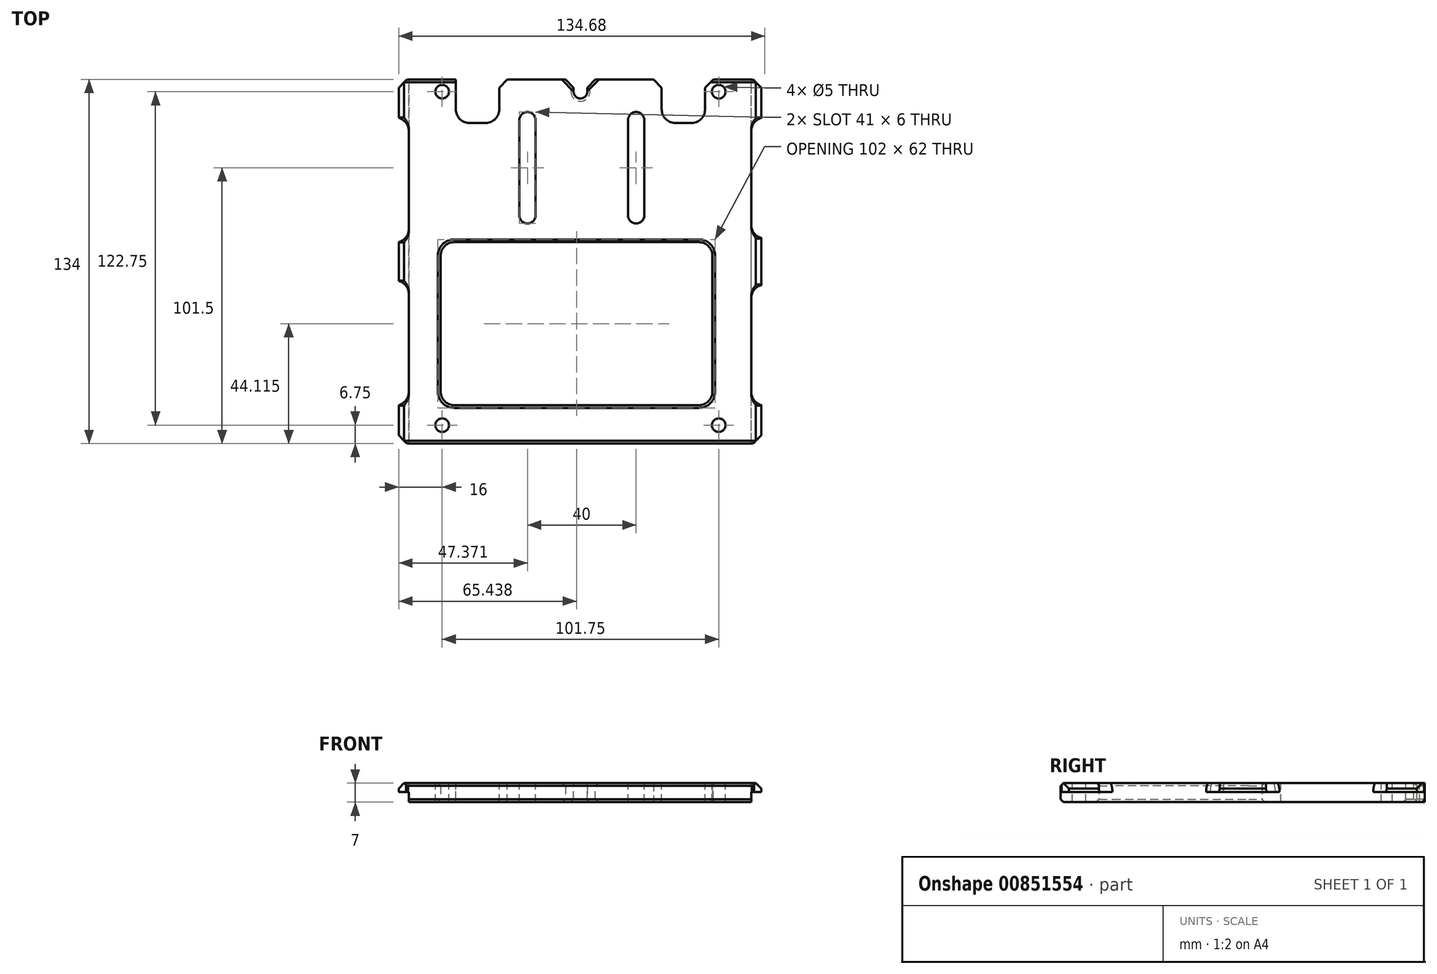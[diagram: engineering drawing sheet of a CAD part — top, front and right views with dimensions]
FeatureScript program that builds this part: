
annotation { "Feature Type Name" : "Feature", "Feature Type Description" : "" }
export const myFeature = defineFeature(function(context is Context, id is Id, definition is map)
    precondition{}
    {
        {
            var Q0;
            Q0=qCreatedBy(makeId("Top.planeOp"),FACE);
            var sketch = newSketch(context, id + "F0", { "sketchPlane" : qUnion([Q0])});
            skLineSegment(sketch, "E0.bottom", {"start": v(0, 0) * mm, "end": v(133.43, 0) * mm});
            skLineSegment(sketch, "E0.top", {"start": v(0, 134) * mm, "end": v(133.43, 134) * mm});
            skLineSegment(sketch, "E0.left", {"start": v(0, 0) * mm, "end": v(0, 134) * mm});
            skLineSegment(sketch, "E0.right", {"start": v(133.43, 0) * mm, "end": v(133.43, 134) * mm});
            skLineSegment(sketch, "E1.bottom", {"start": v(15.44, 74.11) * mm, "end": v(115.44, 74.11) * mm});
            skLineSegment(sketch, "E1.top", {"start": v(15.44, 14.11) * mm, "end": v(115.44, 14.11) * mm});
            skLineSegment(sketch, "E1.left", {"start": v(15.44, 74.11) * mm, "end": v(15.44, 14.11) * mm});
            skLineSegment(sketch, "E1.right", {"start": v(115.44, 74.11) * mm, "end": v(115.44, 14.11) * mm});
            skSolve(sketch);
        }
        {
            var Q0;
            Q0=makeQuery(id+"F0.imprint","IMPRINT",FACE,{"disambiguationData":[TD([[makeQuery(id+"F0.imprint","IMPRINT",EDGE,{"derivedFrom":sQuery(id+"F0.wireOp",EDGE,"E0.bottom")}),1.0]])]});
            extrude(context, id + "F1", {"entities" : qUnion([Q0]), "endBound" : BoundingType.SYMMETRIC, "depth" : 7 * mm, "offsetDistance" : 25 * mm});
        }
        {
            var Q0;
            Q0=makeQuery(id+"F1.opExtrude","CAP_FACE",FACE,{"disambiguationData":[OSD([sQuery(id+"F0.wireOp",EDGE,"E0.bottom"),sQuery(id+"F0.wireOp",EDGE,"E0.top"),sQuery(id+"F0.wireOp",EDGE,"E0.left"),sQuery(id+"F0.wireOp",EDGE,"E0.right")])],"isStart":false});
            var sketch = newSketch(context, id + "F2", { "sketchPlane" : qUnion([Q0])});
            skCircle(sketch, "E2", {"center": v(16, 6.75) * mm, "radius": 2.5 * mm});
            skCircle(sketch, "E3.0.1.0", {"center": v(16, 129.5) * mm, "radius": 2.5 * mm});
            skCircle(sketch, "E3.1.0.0", {"center": v(117.75, 6.75) * mm, "radius": 2.5 * mm});
            skCircle(sketch, "E3.1.1.0", {"center": v(117.75, 129.5) * mm, "radius": 2.5 * mm});
            skLineSegment(sketch, "E3.direction1", {"start": v(16, 6.75) * mm, "end": v(117.75, 6.75) * mm, "construction": true});
            skLineSegment(sketch, "E3.direction2", {"start": v(16, 6.75) * mm, "end": v(16, 129.5) * mm, "construction": true});
            skCircle(sketch, "E4", {"center": v(66.88, 129.5) * mm, "radius": 2.5 * mm});
            skLineSegment(sketch, "E5.bottom", {"start": v(64.38, 129.5) * mm, "end": v(69.34, 129.5) * mm});
            skLineSegment(sketch, "E5.top", {"start": v(64.38, 134) * mm, "end": v(69.34, 134) * mm});
            skLineSegment(sketch, "E5.left", {"start": v(64.38, 129.5) * mm, "end": v(64.38, 134) * mm});
            skLineSegment(sketch, "E5.right", {"start": v(69.34, 129.5) * mm, "end": v(69.34, 134) * mm});
            skLineSegment(sketch, "E6.bottom", {"start": v(21, 134) * mm, "end": v(37, 134) * mm});
            skLineSegment(sketch, "E6.top", {"start": v(21, 118) * mm, "end": v(37, 118) * mm});
            skLineSegment(sketch, "E6.left", {"start": v(21, 134) * mm, "end": v(21, 118) * mm});
            skLineSegment(sketch, "E6.right", {"start": v(37, 134) * mm, "end": v(37, 118) * mm});
            skLineSegment(sketch, "E7.bottom", {"start": v(96.75, 134) * mm, "end": v(112.75, 134) * mm});
            skLineSegment(sketch, "E7.top", {"start": v(96.75, 118) * mm, "end": v(112.75, 118) * mm});
            skLineSegment(sketch, "E7.left", {"start": v(96.75, 134) * mm, "end": v(96.75, 118) * mm});
            skLineSegment(sketch, "E7.right", {"start": v(112.75, 134) * mm, "end": v(112.75, 118) * mm});
            skSolve(sketch);
        }
        {
            var Q0;
            Q0=makeQuery(id+"F2.imprint","IMPRINT",FACE,{"disambiguationData":[TD([[makeQuery(id+"F2.imprint","IMPRINT",EDGE,{"derivedFrom":sQuery(id+"F2.wireOp",EDGE,"E2")}),1.0]])]});
            var Q1;
            Q1=makeQuery(id+"F2.imprint","IMPRINT",FACE,{"disambiguationData":[TD([[makeQuery(id+"F2.imprint","IMPRINT",EDGE,{"derivedFrom":sQuery(id+"F2.wireOp",EDGE,"E3.0.1.0")}),1.0]])]});
            var Q2;
            Q2=makeQuery(id+"F2.imprint","IMPRINT",FACE,{"disambiguationData":[TD([[makeQuery(id+"F2.imprint","IMPRINT",EDGE,{"derivedFrom":sQuery(id+"F2.wireOp",EDGE,"E3.1.1.0")}),1.0]])]});
            var Q3;
            Q3=makeQuery(id+"F2.imprint","IMPRINT",FACE,{"disambiguationData":[TD([[makeQuery(id+"F2.imprint","IMPRINT",EDGE,{"derivedFrom":sQuery(id+"F2.wireOp",EDGE,"E3.1.0.0")}),1.0]])]});
            var Q4;
            Q4=makeQuery(id+"F2.imprint","IMPRINT",FACE,{"disambiguationData":[TD([[makeQuery(id+"F2.imprint","IMPRINT",EDGE,{"derivedFrom":sQuery(id+"F2.wireOp",EDGE,"E4")}),1.0]])]});
            var Q5;
            {var subQ4=sQuery(id+"F2.wireOp",EDGE,"E5.top");Q5=makeQuery(id+"F2.imprint","IMPRINT",FACE,{"disambiguationData":[TD([[makeQuery(id+"F2.imprint","IMPRINT",EDGE,{"derivedFrom":subQ4}),-1.0]])]});}
            var Q6;
            Q6=makeQuery(id+"F2.imprint","IMPRINT",FACE,{"disambiguationData":[TD([[makeQuery(id+"F2.imprint","IMPRINT",EDGE,{"derivedFrom":sQuery(id+"F2.wireOp",EDGE,"E6.bottom")}),-1.0]])]});
            var Q7;
            Q7=makeQuery(id+"F2.imprint","IMPRINT",FACE,{"disambiguationData":[TD([[makeQuery(id+"F2.imprint","IMPRINT",EDGE,{"derivedFrom":sQuery(id+"F2.wireOp",EDGE,"E7.bottom")}),-1.0]])]});
            extrude(context, id + "F3", {"entities" : qUnion([Q0, Q1, Q2, Q3, Q4, Q5, Q6, Q7]), "operationType" : NewBodyOperationType.REMOVE, "oppositeDirection" : true, "depth" : 25 * mm, "offsetDistance" : 25 * mm});
        }
        {
            var Q0;
            Q0=makeQuery(id+"F1.opExtrude","CAP_FACE",FACE,{"disambiguationData":[OSD([sQuery(id+"F0.wireOp",EDGE,"E0.bottom"),sQuery(id+"F0.wireOp",EDGE,"E0.top"),sQuery(id+"F0.wireOp",EDGE,"E0.left"),sQuery(id+"F0.wireOp",EDGE,"E0.right")])],"isStart":false});
            var sketch = newSketch(context, id + "F4", { "sketchPlane" : qUnion([Q0])});
            skLineSegment(sketch, "E8.bottom", {"start": v(0, 120) * mm, "end": v(3.75, 120) * mm});
            skLineSegment(sketch, "E8.top", {"start": v(0, 74) * mm, "end": v(3.75, 74) * mm});
            skLineSegment(sketch, "E8.left", {"start": v(0, 120) * mm, "end": v(0, 74) * mm});
            skLineSegment(sketch, "E8.right", {"start": v(3.75, 120) * mm, "end": v(3.75, 74) * mm});
            skLineSegment(sketch, "E9.bottom", {"start": v(0, 14) * mm, "end": v(3.75, 14) * mm});
            skLineSegment(sketch, "E9.top", {"start": v(0, 60) * mm, "end": v(3.75, 60) * mm});
            skLineSegment(sketch, "E9.left", {"start": v(0, 14) * mm, "end": v(0, 60) * mm});
            skLineSegment(sketch, "E9.right", {"start": v(3.75, 14) * mm, "end": v(3.75, 60) * mm});
            skLineSegment(sketch, "E10.bottom", {"start": v(133.43, 120) * mm, "end": v(129.68, 120) * mm});
            skLineSegment(sketch, "E10.top", {"start": v(133.43, 75.5) * mm, "end": v(129.68, 75.5) * mm});
            skLineSegment(sketch, "E10.left", {"start": v(133.43, 120) * mm, "end": v(133.43, 75.5) * mm});
            skLineSegment(sketch, "E10.right", {"start": v(129.68, 120) * mm, "end": v(129.68, 75.5) * mm});
            skLineSegment(sketch, "E11.bottom", {"start": v(133.43, 14) * mm, "end": v(129.68, 14) * mm});
            skLineSegment(sketch, "E11.top", {"start": v(133.43, 58.5) * mm, "end": v(129.68, 58.5) * mm});
            skLineSegment(sketch, "E11.left", {"start": v(133.43, 14) * mm, "end": v(133.43, 58.5) * mm});
            skLineSegment(sketch, "E11.right", {"start": v(129.68, 14) * mm, "end": v(129.68, 58.5) * mm});
            skSolve(sketch);
        }
        {
            var Q0;
            Q0=makeQuery(id+"F4.imprint","IMPRINT",FACE,{"disambiguationData":[TD([[makeQuery(id+"F4.imprint","IMPRINT",EDGE,{"derivedFrom":sQuery(id+"F4.wireOp",EDGE,"E8.bottom")}),-1.0]])]});
            var Q1;
            Q1=makeQuery(id+"F4.imprint","IMPRINT",FACE,{"disambiguationData":[TD([[makeQuery(id+"F4.imprint","IMPRINT",EDGE,{"derivedFrom":sQuery(id+"F4.wireOp",EDGE,"E9.bottom")}),1.0]])]});
            var Q2;
            Q2=makeQuery(id+"F4.imprint","IMPRINT",FACE,{"disambiguationData":[TD([[makeQuery(id+"F4.imprint","IMPRINT",EDGE,{"derivedFrom":sQuery(id+"F4.wireOp",EDGE,"E11.bottom")}),-1.0]])]});
            var Q3;
            Q3=makeQuery(id+"F4.imprint","IMPRINT",FACE,{"disambiguationData":[TD([[makeQuery(id+"F4.imprint","IMPRINT",EDGE,{"derivedFrom":sQuery(id+"F4.wireOp",EDGE,"E10.bottom")}),1.0]])]});
            extrude(context, id + "F5", {"entities" : qUnion([Q0, Q1, Q2, Q3]), "operationType" : NewBodyOperationType.REMOVE, "oppositeDirection" : true, "depth" : 25 * mm, "offsetDistance" : 25 * mm});
        }
        {
            var Q0;
            Q0=makeQuery(id+"F1.opExtrude","CAP_FACE",FACE,{"disambiguationData":[OSD([sQuery(id+"F0.wireOp",EDGE,"E0.bottom"),sQuery(id+"F0.wireOp",EDGE,"E0.top"),sQuery(id+"F0.wireOp",EDGE,"E0.left"),sQuery(id+"F0.wireOp",EDGE,"E0.right")])],"isStart":true});
            var sketch = newSketch(context, id + "F6", { "sketchPlane" : qUnion([Q0])});
            skLineSegment(sketch, "E12.bottom", {"start": v(0, 0) * mm, "end": v(3.75, 0) * mm});
            skLineSegment(sketch, "E12.top", {"start": v(0, -134) * mm, "end": v(3.75, -134) * mm});
            skLineSegment(sketch, "E12.left", {"start": v(0, 0) * mm, "end": v(0, -134) * mm});
            skLineSegment(sketch, "E12.right", {"start": v(3.75, 0) * mm, "end": v(3.75, -134) * mm});
            skLineSegment(sketch, "E13.bottom", {"start": v(133.43, 0) * mm, "end": v(129.68, 0) * mm});
            skLineSegment(sketch, "E13.top", {"start": v(133.43, -134) * mm, "end": v(129.68, -134) * mm});
            skLineSegment(sketch, "E13.left", {"start": v(133.43, 0) * mm, "end": v(133.43, -134) * mm});
            skLineSegment(sketch, "E13.right", {"start": v(129.68, 0) * mm, "end": v(129.68, -134) * mm});
            skSolve(sketch);
        }
        {
            var Q0;
            Q0=makeQuery(id+"F6.imprint","IMPRINT",FACE,{"disambiguationData":[TD([[makeQuery(id+"F6.imprint","IMPRINT",EDGE,{"derivedFrom":sQuery(id+"F6.wireOp",EDGE,"E12.bottom")}),-1.0]])]});
            var Q1;
            Q1=makeQuery(id+"F6.imprint","IMPRINT",FACE,{"disambiguationData":[TD([[makeQuery(id+"F6.imprint","IMPRINT",EDGE,{"derivedFrom":sQuery(id+"F6.wireOp",EDGE,"E13.bottom")}),-1.0]])]});
            var Q2;
            {var subQ1=makeQuery(id+"F1.opExtrude","CAP_FACE",FACE,{"disambiguationData":[OSD([sQuery(id+"F0.wireOp",EDGE,"E0.bottom"),sQuery(id+"F0.wireOp",EDGE,"E0.top"),sQuery(id+"F0.wireOp",EDGE,"E0.left"),sQuery(id+"F0.wireOp",EDGE,"E0.right")])],"isStart":true});var subQ2=makeQuery(id+"F5.boolean.opBoolean","INTERSECT",EDGE,{"derivedFrom":[subQ1,makeQuery(id+"F5.opExtrude","SWEPT_FACE",FACE,{"disambiguationData":[OSD([sQuery(id+"F4.wireOp",EDGE,"E8.top")])]})]});Q2=makeQuery(id+"F6.imprint","IMPRINT",FACE,{"disambiguationData":[TD([[makeQuery(id+"F6.imprint","IMPRINT",EDGE,{"derivedFrom":subQ2}),1.0]])]});}
            var Q3;
            {var subQ0=sQuery(id+"F6.wireOp",EDGE,"E12.top");Q3=makeQuery(id+"F6.imprint","IMPRINT",FACE,{"disambiguationData":[TD([[makeQuery(id+"F6.imprint","IMPRINT",EDGE,{"derivedFrom":subQ0}),1.0]])]});}
            var Q4;
            {var subQ0=sQuery(id+"F6.wireOp",EDGE,"E13.top");Q4=makeQuery(id+"F6.imprint","IMPRINT",FACE,{"disambiguationData":[TD([[makeQuery(id+"F6.imprint","IMPRINT",EDGE,{"derivedFrom":subQ0}),1.0]])]});}
            var Q5;
            {var subQ1=makeQuery(id+"F1.opExtrude","CAP_FACE",FACE,{"disambiguationData":[OSD([sQuery(id+"F0.wireOp",EDGE,"E0.bottom"),sQuery(id+"F0.wireOp",EDGE,"E0.top"),sQuery(id+"F0.wireOp",EDGE,"E0.left"),sQuery(id+"F0.wireOp",EDGE,"E0.right")])],"isStart":true});var subQ2=makeQuery(id+"F5.boolean.opBoolean","INTERSECT",EDGE,{"derivedFrom":[subQ1,makeQuery(id+"F5.opExtrude","SWEPT_FACE",FACE,{"disambiguationData":[OSD([sQuery(id+"F4.wireOp",EDGE,"E10.top")])]})]});Q5=makeQuery(id+"F6.imprint","IMPRINT",FACE,{"disambiguationData":[TD([[makeQuery(id+"F6.imprint","IMPRINT",EDGE,{"derivedFrom":subQ2}),-1.0]])]});}
            extrude(context, id + "F7", {"entities" : qUnion([Q0, Q1, Q2, Q3, Q4, Q5]), "operationType" : NewBodyOperationType.REMOVE, "oppositeDirection" : true, "depth" : 3.75 * mm, "offsetDistance" : 25 * mm});
        }
        {
            var Q0;
            {var subQ0=sQuery(id+"F0.wireOp",EDGE,"E0.left");var subQ1=sQuery(id+"F0.wireOp",EDGE,"E0.top");Q0=makeQuery(id+"F5.boolean.opBoolean","SPLIT",EDGE,{"disambiguationData":[TD([makeQuery(id+"F1.opExtrude","SWEPT_FACE",FACE,{"disambiguationData":[OSD([subQ1])]})])],"derivedFrom":makeQuery(id+"F1.opExtrude","CAP_EDGE",EDGE,{"disambiguationData":[OSD([subQ0])],"isStart":false})});}
            var Q1;
            {var subQ0=sQuery(id+"F0.wireOp",EDGE,"E0.left");Q1=makeQuery(id+"F5.boolean.opBoolean","SPLIT",EDGE,{"disambiguationData":[TD([makeQuery(id+"F5.opExtrude","SWEPT_FACE",FACE,{"disambiguationData":[OSD([sQuery(id+"F4.wireOp",EDGE,"E8.top")])]})])],"derivedFrom":makeQuery(id+"F1.opExtrude","CAP_EDGE",EDGE,{"disambiguationData":[OSD([subQ0])],"isStart":false})});}
            var Q2;
            {var subQ0=sQuery(id+"F0.wireOp",EDGE,"E0.bottom");var subQ1=sQuery(id+"F0.wireOp",EDGE,"E0.left");Q2=makeQuery(id+"F5.boolean.opBoolean","SPLIT",EDGE,{"disambiguationData":[TD([makeQuery(id+"F1.opExtrude","SWEPT_FACE",FACE,{"disambiguationData":[OSD([subQ0])]})])],"derivedFrom":makeQuery(id+"F1.opExtrude","CAP_EDGE",EDGE,{"disambiguationData":[OSD([subQ1])],"isStart":false})});}
            var Q3;
            {var subQ0=sQuery(id+"F0.wireOp",EDGE,"E0.bottom");var subQ1=sQuery(id+"F0.wireOp",EDGE,"E0.right");Q3=makeQuery(id+"F5.boolean.opBoolean","SPLIT",EDGE,{"disambiguationData":[TD([makeQuery(id+"F1.opExtrude","SWEPT_FACE",FACE,{"disambiguationData":[OSD([subQ0])]})])],"derivedFrom":makeQuery(id+"F1.opExtrude","CAP_EDGE",EDGE,{"disambiguationData":[OSD([subQ1])],"isStart":false})});}
            var Q4;
            {var subQ0=sQuery(id+"F0.wireOp",EDGE,"E0.right");Q4=makeQuery(id+"F5.boolean.opBoolean","SPLIT",EDGE,{"disambiguationData":[TD([makeQuery(id+"F5.opExtrude","SWEPT_FACE",FACE,{"disambiguationData":[OSD([sQuery(id+"F4.wireOp",EDGE,"E10.top")])]})])],"derivedFrom":makeQuery(id+"F1.opExtrude","CAP_EDGE",EDGE,{"disambiguationData":[OSD([subQ0])],"isStart":false})});}
            var Q5;
            {var subQ0=sQuery(id+"F0.wireOp",EDGE,"E0.right");var subQ1=sQuery(id+"F0.wireOp",EDGE,"E0.top");Q5=makeQuery(id+"F5.boolean.opBoolean","SPLIT",EDGE,{"disambiguationData":[TD([makeQuery(id+"F1.opExtrude","SWEPT_FACE",FACE,{"disambiguationData":[OSD([subQ1])]})])],"derivedFrom":makeQuery(id+"F1.opExtrude","CAP_EDGE",EDGE,{"disambiguationData":[OSD([subQ0])],"isStart":false})});}
            chamfer(context, id + "F8", {"entities" : qUnion([Q0, Q1, Q2, Q3, Q4, Q5]), "width" : 2 * mm, "tangentPropagation" : true});
        }
        {
            var Q0;
            Q0=makeQuery(id+"F3.boolean.opBoolean","COPY",EDGE,{"derivedFrom":makeQuery(id+"F3.opExtrude","SWEPT_EDGE",EDGE,{"disambiguationData":[OSD([sQuery(id+"F0.wireOp",EDGE,"E0.top"),sQuery(id+"F2.wireOp",EDGE,"E5.top"),sQuery(id+"F2.wireOp",EDGE,"E5.left")])]})});
            var Q1;
            Q1=makeQuery(id+"F3.boolean.opBoolean","COPY",EDGE,{"derivedFrom":makeQuery(id+"F3.opExtrude","SWEPT_EDGE",EDGE,{"disambiguationData":[OSD([sQuery(id+"F0.wireOp",EDGE,"E0.top"),sQuery(id+"F2.wireOp",EDGE,"E5.top"),sQuery(id+"F2.wireOp",EDGE,"E5.right")])]})});
            var Q2;
            Q2=makeQuery(id+"F1.opExtrude","SWEPT_EDGE",EDGE,{"disambiguationData":[OSD([sQuery(id+"F0.wireOp",EDGE,"E0.top"),sQuery(id+"F0.wireOp",EDGE,"E0.left")])]});
            var Q3;
            Q3=makeQuery(id+"F1.opExtrude","SWEPT_EDGE",EDGE,{"disambiguationData":[OSD([sQuery(id+"F0.wireOp",EDGE,"E0.top"),sQuery(id+"F0.wireOp",EDGE,"E0.right")])]});
            var Q4;
            Q4=makeQuery(id+"F1.opExtrude","SWEPT_EDGE",EDGE,{"disambiguationData":[OSD([sQuery(id+"F0.wireOp",EDGE,"E0.bottom"),sQuery(id+"F0.wireOp",EDGE,"E0.left")])]});
            var Q5;
            Q5=makeQuery(id+"F1.opExtrude","SWEPT_EDGE",EDGE,{"disambiguationData":[OSD([sQuery(id+"F0.wireOp",EDGE,"E0.bottom"),sQuery(id+"F0.wireOp",EDGE,"E0.right")])]});
            var Q6;
            Q6=makeQuery(id+"F3.boolean.opBoolean","COPY",EDGE,{"derivedFrom":makeQuery(id+"F3.opExtrude","SWEPT_EDGE",EDGE,{"disambiguationData":[OSD([sQuery(id+"F0.wireOp",EDGE,"E0.top"),sQuery(id+"F2.wireOp",EDGE,"E6.bottom"),sQuery(id+"F2.wireOp",EDGE,"E6.left")])]})});
            var Q7;
            Q7=makeQuery(id+"F3.boolean.opBoolean","COPY",EDGE,{"derivedFrom":makeQuery(id+"F3.opExtrude","SWEPT_EDGE",EDGE,{"disambiguationData":[OSD([sQuery(id+"F0.wireOp",EDGE,"E0.top"),sQuery(id+"F2.wireOp",EDGE,"E6.bottom"),sQuery(id+"F2.wireOp",EDGE,"E6.right")])]})});
            var Q8;
            Q8=makeQuery(id+"F3.boolean.opBoolean","COPY",EDGE,{"derivedFrom":makeQuery(id+"F3.opExtrude","SWEPT_EDGE",EDGE,{"disambiguationData":[OSD([sQuery(id+"F0.wireOp",EDGE,"E0.top"),sQuery(id+"F2.wireOp",EDGE,"E7.bottom"),sQuery(id+"F2.wireOp",EDGE,"E7.left")])]})});
            var Q9;
            Q9=makeQuery(id+"F3.boolean.opBoolean","COPY",EDGE,{"derivedFrom":makeQuery(id+"F3.opExtrude","SWEPT_EDGE",EDGE,{"disambiguationData":[OSD([sQuery(id+"F0.wireOp",EDGE,"E0.top"),sQuery(id+"F2.wireOp",EDGE,"E7.bottom"),sQuery(id+"F2.wireOp",EDGE,"E7.right")])]})});
            chamfer(context, id + "F9", {"entities" : qUnion([Q0, Q1, Q2, Q3, Q4, Q5, Q6, Q7, Q8, Q9]), "width" : 3 * mm, "tangentPropagation" : true});
        }
        {
            var Q0;
            Q0=makeQuery(id+"F5.boolean.opBoolean","COPY",EDGE,{"derivedFrom":makeQuery(id+"F5.opExtrude","SWEPT_EDGE",EDGE,{"disambiguationData":[OSD([sQuery(id+"F4.wireOp",EDGE,"E8.bottom"),sQuery(id+"F4.wireOp",EDGE,"E8.right")])]})});
            var Q1;
            Q1=makeQuery(id+"F5.boolean.opBoolean","COPY",EDGE,{"derivedFrom":makeQuery(id+"F5.opExtrude","SWEPT_EDGE",EDGE,{"disambiguationData":[OSD([sQuery(id+"F4.wireOp",EDGE,"E8.top"),sQuery(id+"F4.wireOp",EDGE,"E8.right")])]})});
            var Q2;
            Q2=makeQuery(id+"F5.boolean.opBoolean","COPY",EDGE,{"derivedFrom":makeQuery(id+"F5.opExtrude","SWEPT_EDGE",EDGE,{"disambiguationData":[OSD([sQuery(id+"F4.wireOp",EDGE,"E9.bottom"),sQuery(id+"F4.wireOp",EDGE,"E9.right")])]})});
            var Q3;
            Q3=makeQuery(id+"F5.boolean.opBoolean","COPY",EDGE,{"derivedFrom":makeQuery(id+"F5.opExtrude","SWEPT_EDGE",EDGE,{"disambiguationData":[OSD([sQuery(id+"F4.wireOp",EDGE,"E9.top"),sQuery(id+"F4.wireOp",EDGE,"E9.right")])]})});
            var Q4;
            Q4=makeQuery(id+"F5.boolean.opBoolean","COPY",EDGE,{"derivedFrom":makeQuery(id+"F5.opExtrude","SWEPT_EDGE",EDGE,{"disambiguationData":[OSD([sQuery(id+"F4.wireOp",EDGE,"E11.bottom"),sQuery(id+"F4.wireOp",EDGE,"E11.right")])]})});
            var Q5;
            Q5=makeQuery(id+"F5.boolean.opBoolean","COPY",EDGE,{"derivedFrom":makeQuery(id+"F5.opExtrude","SWEPT_EDGE",EDGE,{"disambiguationData":[OSD([sQuery(id+"F4.wireOp",EDGE,"E10.top"),sQuery(id+"F4.wireOp",EDGE,"E10.right")])]})});
            var Q6;
            Q6=makeQuery(id+"F5.boolean.opBoolean","COPY",EDGE,{"derivedFrom":makeQuery(id+"F5.opExtrude","SWEPT_EDGE",EDGE,{"disambiguationData":[OSD([sQuery(id+"F4.wireOp",EDGE,"E10.bottom"),sQuery(id+"F4.wireOp",EDGE,"E10.right")])]})});
            var Q7;
            Q7=makeQuery(id+"F5.boolean.opBoolean","COPY",EDGE,{"derivedFrom":makeQuery(id+"F5.opExtrude","SWEPT_EDGE",EDGE,{"disambiguationData":[OSD([sQuery(id+"F4.wireOp",EDGE,"E11.top"),sQuery(id+"F4.wireOp",EDGE,"E11.right")])]})});
            var Q8;
            Q8=makeQuery(id+"F1.opExtrude","SWEPT_EDGE",EDGE,{"disambiguationData":[OSD([sQuery(id+"F0.wireOp",EDGE,"E1.bottom"),sQuery(id+"F0.wireOp",EDGE,"E1.left")])]});
            var Q9;
            Q9=makeQuery(id+"F1.opExtrude","SWEPT_EDGE",EDGE,{"disambiguationData":[OSD([sQuery(id+"F0.wireOp",EDGE,"E1.top"),sQuery(id+"F0.wireOp",EDGE,"E1.left")])]});
            var Q10;
            Q10=makeQuery(id+"F1.opExtrude","SWEPT_EDGE",EDGE,{"disambiguationData":[OSD([sQuery(id+"F0.wireOp",EDGE,"E1.bottom"),sQuery(id+"F0.wireOp",EDGE,"E1.right")])]});
            var Q11;
            Q11=makeQuery(id+"F1.opExtrude","SWEPT_EDGE",EDGE,{"disambiguationData":[OSD([sQuery(id+"F0.wireOp",EDGE,"E1.top"),sQuery(id+"F0.wireOp",EDGE,"E1.right")])]});
            var Q12;
            Q12=makeQuery(id+"F3.boolean.opBoolean","COPY",EDGE,{"derivedFrom":makeQuery(id+"F3.opExtrude","SWEPT_EDGE",EDGE,{"disambiguationData":[OSD([sQuery(id+"F2.wireOp",EDGE,"E6.top"),sQuery(id+"F2.wireOp",EDGE,"E6.left")])]})});
            var Q13;
            Q13=makeQuery(id+"F3.boolean.opBoolean","COPY",EDGE,{"derivedFrom":makeQuery(id+"F3.opExtrude","SWEPT_EDGE",EDGE,{"disambiguationData":[OSD([sQuery(id+"F2.wireOp",EDGE,"E7.top"),sQuery(id+"F2.wireOp",EDGE,"E7.left")])]})});
            var Q14;
            Q14=makeQuery(id+"F3.boolean.opBoolean","COPY",EDGE,{"derivedFrom":makeQuery(id+"F3.opExtrude","SWEPT_EDGE",EDGE,{"disambiguationData":[OSD([sQuery(id+"F2.wireOp",EDGE,"E6.top"),sQuery(id+"F2.wireOp",EDGE,"E6.right")])]})});
            var Q15;
            Q15=makeQuery(id+"F3.boolean.opBoolean","COPY",EDGE,{"derivedFrom":makeQuery(id+"F3.opExtrude","SWEPT_EDGE",EDGE,{"disambiguationData":[OSD([sQuery(id+"F2.wireOp",EDGE,"E7.top"),sQuery(id+"F2.wireOp",EDGE,"E7.right")])]})});
            fillet(context, id + "F10", {"entities" : qUnion([Q0, Q1, Q2, Q3, Q4, Q5, Q6, Q7, Q8, Q9, Q10, Q11, Q12, Q13, Q14, Q15]), "radius" : 5 * mm, "tangentPropagation" : true, "allowEdgeOverflow" : false});
        }
        {
            var Q0;
            Q0=makeQuery(id+"F1.opExtrude","CAP_EDGE",EDGE,{"disambiguationData":[OSD([sQuery(id+"F0.wireOp",EDGE,"E0.bottom")])],"isStart":false});
            var Q1;
            Q1=makeQuery(id+"F1.opExtrude","CAP_EDGE",EDGE,{"disambiguationData":[OSD([sQuery(id+"F0.wireOp",EDGE,"E0.bottom")])],"isStart":true});
            var Q2;
            Q2=makeQuery(id+"F7.boolean.opBoolean","COPY",EDGE,{"derivedFrom":makeQuery(id+"F7.opExtrude","SWEPT_EDGE",EDGE,{"disambiguationData":[OSD([sQuery(id+"F0.wireOp",EDGE,"E0.bottom"),sQuery(id+"F6.wireOp",EDGE,"E13.bottom"),sQuery(id+"F6.wireOp",EDGE,"E13.right")])]})});
            var Q3;
            Q3=makeQuery(id+"F7.boolean.opBoolean","COPY",EDGE,{"derivedFrom":makeQuery(id+"F7.opExtrude","SWEPT_EDGE",EDGE,{"disambiguationData":[OSD([sQuery(id+"F0.wireOp",EDGE,"E0.bottom"),sQuery(id+"F6.wireOp",EDGE,"E12.bottom"),sQuery(id+"F6.wireOp",EDGE,"E12.right")])]})});
            var Q4;
            Q4=makeQuery(id+"F7.boolean.opBoolean","COPY",EDGE,{"derivedFrom":makeQuery(id+"F7.opExtrude","SWEPT_EDGE",EDGE,{"disambiguationData":[OSD([sQuery(id+"F0.wireOp",EDGE,"E0.top"),sQuery(id+"F6.wireOp",EDGE,"E12.top"),sQuery(id+"F6.wireOp",EDGE,"E12.right")])]})});
            var Q5;
            {var subQ0=sQuery(id+"F0.wireOp",EDGE,"E0.left");var subQ1=sQuery(id+"F0.wireOp",EDGE,"E0.top");Q5=makeQuery(id+"F3.boolean.opBoolean","SPLIT",EDGE,{"disambiguationData":[TD([makeQuery(id+"F1.opExtrude","SWEPT_FACE",FACE,{"disambiguationData":[OSD([subQ0])]})])],"derivedFrom":makeQuery(id+"F1.opExtrude","CAP_EDGE",EDGE,{"disambiguationData":[OSD([subQ1])],"isStart":false})});}
            var Q6;
            Q6=makeQuery(id+"F3.boolean.opBoolean","COPY",EDGE,{"derivedFrom":makeQuery(id+"F3.opExtrude","CAP_EDGE",EDGE,{"disambiguationData":[OSD([sQuery(id+"F2.wireOp",EDGE,"E4")])],"isStart":true})});
            var Q7;
            {var subQ0=sQuery(id+"F0.wireOp",EDGE,"E0.top");Q7=makeQuery(id+"F9.opChamfer","BLEND_EDGE",EDGE,{"blendedFrom":[makeQuery(id+"F3.boolean.opBoolean","COPY",EDGE,{"derivedFrom":makeQuery(id+"F3.opExtrude","SWEPT_EDGE",EDGE,{"disambiguationData":[OSD([subQ0,sQuery(id+"F2.wireOp",EDGE,"E5.top"),sQuery(id+"F2.wireOp",EDGE,"E5.left")])]})}),makeQuery(id+"F1.opExtrude","CAP_FACE",FACE,{"disambiguationData":[OSD([sQuery(id+"F0.wireOp",EDGE,"E0.bottom"),subQ0,sQuery(id+"F0.wireOp",EDGE,"E0.left"),sQuery(id+"F0.wireOp",EDGE,"E0.right")])],"isStart":false})],"blendedInto":[makeQuery(id+"F1.opExtrude","CAP_FACE",FACE,{"disambiguationData":[OSD([sQuery(id+"F0.wireOp",EDGE,"E0.bottom"),subQ0,sQuery(id+"F0.wireOp",EDGE,"E0.left"),sQuery(id+"F0.wireOp",EDGE,"E0.right")])],"isStart":false})]});}
            var Q8;
            {var subQ0=sQuery(id+"F0.wireOp",EDGE,"E0.top");Q8=makeQuery(id+"F9.opChamfer","BLEND_EDGE",EDGE,{"blendedFrom":[makeQuery(id+"F3.boolean.opBoolean","COPY",EDGE,{"derivedFrom":makeQuery(id+"F3.opExtrude","SWEPT_EDGE",EDGE,{"disambiguationData":[OSD([subQ0,sQuery(id+"F2.wireOp",EDGE,"E5.top"),sQuery(id+"F2.wireOp",EDGE,"E5.right")])]})}),makeQuery(id+"F1.opExtrude","CAP_FACE",FACE,{"disambiguationData":[OSD([sQuery(id+"F0.wireOp",EDGE,"E0.bottom"),subQ0,sQuery(id+"F0.wireOp",EDGE,"E0.left"),sQuery(id+"F0.wireOp",EDGE,"E0.right")])],"isStart":false})],"blendedInto":[makeQuery(id+"F1.opExtrude","CAP_FACE",FACE,{"disambiguationData":[OSD([sQuery(id+"F0.wireOp",EDGE,"E0.bottom"),subQ0,sQuery(id+"F0.wireOp",EDGE,"E0.left"),sQuery(id+"F0.wireOp",EDGE,"E0.right")])],"isStart":false})]});}
            var Q9;
            {var subQ0=sQuery(id+"F0.wireOp",EDGE,"E0.top");Q9=makeQuery(id+"F9.opChamfer","BLEND_EDGE",EDGE,{"blendedFrom":[makeQuery(id+"F3.boolean.opBoolean","COPY",EDGE,{"derivedFrom":makeQuery(id+"F3.opExtrude","SWEPT_EDGE",EDGE,{"disambiguationData":[OSD([subQ0,sQuery(id+"F2.wireOp",EDGE,"E5.top"),sQuery(id+"F2.wireOp",EDGE,"E5.right")])]})}),makeQuery(id+"F1.opExtrude","CAP_FACE",FACE,{"disambiguationData":[OSD([sQuery(id+"F0.wireOp",EDGE,"E0.bottom"),subQ0,sQuery(id+"F0.wireOp",EDGE,"E0.left"),sQuery(id+"F0.wireOp",EDGE,"E0.right")])],"isStart":true})],"blendedInto":[makeQuery(id+"F1.opExtrude","CAP_FACE",FACE,{"disambiguationData":[OSD([sQuery(id+"F0.wireOp",EDGE,"E0.bottom"),subQ0,sQuery(id+"F0.wireOp",EDGE,"E0.left"),sQuery(id+"F0.wireOp",EDGE,"E0.right")])],"isStart":true})]});}
            var Q10;
            Q10=makeQuery(id+"F3.boolean.opBoolean","INTERSECT",EDGE,{"derivedFrom":[makeQuery(id+"F1.opExtrude","CAP_FACE",FACE,{"disambiguationData":[OSD([sQuery(id+"F0.wireOp",EDGE,"E0.bottom"),sQuery(id+"F0.wireOp",EDGE,"E0.top"),sQuery(id+"F0.wireOp",EDGE,"E0.left"),sQuery(id+"F0.wireOp",EDGE,"E0.right")])],"isStart":true}),makeQuery(id+"F3.opExtrude","SWEPT_FACE",FACE,{"disambiguationData":[OSD([sQuery(id+"F2.wireOp",EDGE,"E4")])]})]});
            var Q11;
            {var subQ0=sQuery(id+"F0.wireOp",EDGE,"E0.top");Q11=makeQuery(id+"F9.opChamfer","BLEND_EDGE",EDGE,{"blendedFrom":[makeQuery(id+"F3.boolean.opBoolean","COPY",EDGE,{"derivedFrom":makeQuery(id+"F3.opExtrude","SWEPT_EDGE",EDGE,{"disambiguationData":[OSD([subQ0,sQuery(id+"F2.wireOp",EDGE,"E5.top"),sQuery(id+"F2.wireOp",EDGE,"E5.left")])]})}),makeQuery(id+"F1.opExtrude","CAP_FACE",FACE,{"disambiguationData":[OSD([sQuery(id+"F0.wireOp",EDGE,"E0.bottom"),subQ0,sQuery(id+"F0.wireOp",EDGE,"E0.left"),sQuery(id+"F0.wireOp",EDGE,"E0.right")])],"isStart":true})],"blendedInto":[makeQuery(id+"F1.opExtrude","CAP_FACE",FACE,{"disambiguationData":[OSD([sQuery(id+"F0.wireOp",EDGE,"E0.bottom"),subQ0,sQuery(id+"F0.wireOp",EDGE,"E0.left"),sQuery(id+"F0.wireOp",EDGE,"E0.right")])],"isStart":true})]});}
            var Q12;
            {var subQ0=sQuery(id+"F0.wireOp",EDGE,"E0.right");var subQ1=sQuery(id+"F0.wireOp",EDGE,"E0.top");Q12=makeQuery(id+"F3.boolean.opBoolean","SPLIT",EDGE,{"disambiguationData":[TD([makeQuery(id+"F1.opExtrude","SWEPT_FACE",FACE,{"disambiguationData":[OSD([subQ0])]})])],"derivedFrom":makeQuery(id+"F1.opExtrude","CAP_EDGE",EDGE,{"disambiguationData":[OSD([subQ1])],"isStart":false})});}
            var Q13;
            {var subQ0=sQuery(id+"F0.wireOp",EDGE,"E0.right");var subQ1=sQuery(id+"F0.wireOp",EDGE,"E0.top");Q13=makeQuery(id+"F3.boolean.opBoolean","SPLIT",EDGE,{"disambiguationData":[TD([makeQuery(id+"F1.opExtrude","SWEPT_FACE",FACE,{"disambiguationData":[OSD([subQ0])]})])],"derivedFrom":makeQuery(id+"F1.opExtrude","CAP_EDGE",EDGE,{"disambiguationData":[OSD([subQ1])],"isStart":true})});}
            var Q14;
            Q14=makeQuery(id+"F7.boolean.opBoolean","COPY",EDGE,{"derivedFrom":makeQuery(id+"F7.opExtrude","SWEPT_EDGE",EDGE,{"disambiguationData":[OSD([sQuery(id+"F0.wireOp",EDGE,"E0.top"),sQuery(id+"F6.wireOp",EDGE,"E13.top"),sQuery(id+"F6.wireOp",EDGE,"E13.right")])]})});
            var Q15;
            {var subQ0=sQuery(id+"F6.wireOp",EDGE,"E13.right");var subQ1=sQuery(id+"F0.wireOp",EDGE,"E0.right");var subQ2=sQuery(id+"F0.wireOp",EDGE,"E0.top");var subQ3=sQuery(id+"F0.wireOp",EDGE,"E0.bottom");var subQ4=makeQuery(id+"F1.opExtrude","CAP_FACE",FACE,{"disambiguationData":[OSD([subQ3,subQ2,sQuery(id+"F0.wireOp",EDGE,"E0.left"),subQ1])],"isStart":true});var subQ5=subQ4;Q15=makeQuery(id+"F7.boolean.opBoolean","MERGE",EDGE,{"derivedFrom":[makeQuery(id+"F5.boolean.opBoolean","INTERSECT",EDGE,{"derivedFrom":[subQ5,makeQuery(id+"F5.opExtrude","SWEPT_FACE",FACE,{"disambiguationData":[OSD([sQuery(id+"F4.wireOp",EDGE,"E10.right")])]})]}),makeQuery(id+"F5.boolean.opBoolean","INTERSECT",EDGE,{"derivedFrom":[subQ5,makeQuery(id+"F5.opExtrude","SWEPT_FACE",FACE,{"disambiguationData":[OSD([sQuery(id+"F4.wireOp",EDGE,"E11.right")])]})]}),makeQuery(id+"F7.opExtrude","CAP_EDGE",EDGE,{"disambiguationData":[OSD([subQ0]),TDD([makeQuery(id+"F6.imprint","IMPRINT",EDGE,{"disambiguationData":[TD([[makeQuery(id+"F6.imprint","INTERSECT",VERTEX,{"derivedFrom":[makeQuery(id+"F5.boolean.opBoolean","INTERSECT",EDGE,{"derivedFrom":[subQ5,makeQuery(id+"F5.opExtrude","SWEPT_FACE",FACE,{"disambiguationData":[OSD([sQuery(id+"F4.wireOp",EDGE,"E11.bottom")])]})]}),subQ0]}),1.0],[makeQuery(id+"F6.imprint","INTERSECT",VERTEX,{"derivedFrom":[makeQuery(id+"F1.opExtrude","CAP_EDGE",EDGE,{"disambiguationData":[OSD([subQ3])],"isStart":true}),sQuery(id+"F6.wireOp",EDGE,"E13.bottom"),subQ0]}),-1.0]])],"derivedFrom":subQ0})])],"isStart":true}),makeQuery(id+"F7.opExtrude","CAP_EDGE",EDGE,{"disambiguationData":[OSD([subQ0]),TDD([makeQuery(id+"F6.imprint","IMPRINT",EDGE,{"disambiguationData":[TD([[makeQuery(id+"F6.imprint","INTERSECT",VERTEX,{"derivedFrom":[makeQuery(id+"F5.boolean.opBoolean","INTERSECT",EDGE,{"derivedFrom":[subQ5,makeQuery(id+"F5.opExtrude","SWEPT_FACE",FACE,{"disambiguationData":[OSD([sQuery(id+"F4.wireOp",EDGE,"E10.top")])]})]}),subQ0]}),1.0],[makeQuery(id+"F6.imprint","INTERSECT",VERTEX,{"derivedFrom":[makeQuery(id+"F5.boolean.opBoolean","INTERSECT",EDGE,{"derivedFrom":[subQ5,makeQuery(id+"F5.opExtrude","SWEPT_FACE",FACE,{"disambiguationData":[OSD([sQuery(id+"F4.wireOp",EDGE,"E11.top")])]})]}),subQ0]}),-1.0]])],"derivedFrom":subQ0})])],"isStart":true}),makeQuery(id+"F7.opExtrude","CAP_EDGE",EDGE,{"disambiguationData":[OSD([subQ0]),TDD([makeQuery(id+"F6.imprint","IMPRINT",EDGE,{"disambiguationData":[TD([[makeQuery(id+"F6.imprint","INTERSECT",VERTEX,{"derivedFrom":[makeQuery(id+"F5.boolean.opBoolean","INTERSECT",EDGE,{"derivedFrom":[subQ5,makeQuery(id+"F5.opExtrude","SWEPT_FACE",FACE,{"disambiguationData":[OSD([sQuery(id+"F4.wireOp",EDGE,"E10.bottom")])]})]}),subQ0]}),-1.0],[makeQuery(id+"F6.imprint","INTERSECT",VERTEX,{"derivedFrom":[makeQuery(id+"F3.boolean.opBoolean","SPLIT",EDGE,{"disambiguationData":[TD([makeQuery(id+"F1.opExtrude","SWEPT_FACE",FACE,{"disambiguationData":[OSD([subQ1])]})])],"derivedFrom":makeQuery(id+"F1.opExtrude","CAP_EDGE",EDGE,{"disambiguationData":[OSD([subQ2])],"isStart":true})}),sQuery(id+"F6.wireOp",EDGE,"E13.top"),subQ0]}),1.0]])],"derivedFrom":subQ0})])],"isStart":true})]});}
            var Q16;
            {var subQ0=sQuery(id+"F6.wireOp",EDGE,"E12.right");var subQ1=sQuery(id+"F0.wireOp",EDGE,"E0.left");var subQ2=sQuery(id+"F0.wireOp",EDGE,"E0.top");var subQ3=sQuery(id+"F0.wireOp",EDGE,"E0.bottom");var subQ4=makeQuery(id+"F1.opExtrude","CAP_FACE",FACE,{"disambiguationData":[OSD([subQ3,subQ2,subQ1,sQuery(id+"F0.wireOp",EDGE,"E0.right")])],"isStart":true});var subQ5=subQ4;Q16=makeQuery(id+"F7.boolean.opBoolean","MERGE",EDGE,{"derivedFrom":[makeQuery(id+"F5.boolean.opBoolean","INTERSECT",EDGE,{"derivedFrom":[subQ5,makeQuery(id+"F5.opExtrude","SWEPT_FACE",FACE,{"disambiguationData":[OSD([sQuery(id+"F4.wireOp",EDGE,"E8.right")])]})]}),makeQuery(id+"F5.boolean.opBoolean","INTERSECT",EDGE,{"derivedFrom":[subQ5,makeQuery(id+"F5.opExtrude","SWEPT_FACE",FACE,{"disambiguationData":[OSD([sQuery(id+"F4.wireOp",EDGE,"E9.right")])]})]}),makeQuery(id+"F7.opExtrude","CAP_EDGE",EDGE,{"disambiguationData":[OSD([subQ0]),TDD([makeQuery(id+"F6.imprint","IMPRINT",EDGE,{"disambiguationData":[TD([[makeQuery(id+"F6.imprint","INTERSECT",VERTEX,{"derivedFrom":[makeQuery(id+"F5.boolean.opBoolean","INTERSECT",EDGE,{"derivedFrom":[subQ5,makeQuery(id+"F5.opExtrude","SWEPT_FACE",FACE,{"disambiguationData":[OSD([sQuery(id+"F4.wireOp",EDGE,"E9.bottom")])]})]}),subQ0]}),1.0],[makeQuery(id+"F6.imprint","INTERSECT",VERTEX,{"derivedFrom":[makeQuery(id+"F1.opExtrude","CAP_EDGE",EDGE,{"disambiguationData":[OSD([subQ3])],"isStart":true}),sQuery(id+"F6.wireOp",EDGE,"E12.bottom"),subQ0]}),-1.0]])],"derivedFrom":subQ0})])],"isStart":true}),makeQuery(id+"F7.opExtrude","CAP_EDGE",EDGE,{"disambiguationData":[OSD([subQ0]),TDD([makeQuery(id+"F6.imprint","IMPRINT",EDGE,{"disambiguationData":[TD([[makeQuery(id+"F6.imprint","INTERSECT",VERTEX,{"derivedFrom":[makeQuery(id+"F5.boolean.opBoolean","INTERSECT",EDGE,{"derivedFrom":[subQ5,makeQuery(id+"F5.opExtrude","SWEPT_FACE",FACE,{"disambiguationData":[OSD([sQuery(id+"F4.wireOp",EDGE,"E8.top")])]})]}),subQ0]}),1.0],[makeQuery(id+"F6.imprint","INTERSECT",VERTEX,{"derivedFrom":[makeQuery(id+"F5.boolean.opBoolean","INTERSECT",EDGE,{"derivedFrom":[subQ5,makeQuery(id+"F5.opExtrude","SWEPT_FACE",FACE,{"disambiguationData":[OSD([sQuery(id+"F4.wireOp",EDGE,"E9.top")])]})]}),subQ0]}),-1.0]])],"derivedFrom":subQ0})])],"isStart":true}),makeQuery(id+"F7.opExtrude","CAP_EDGE",EDGE,{"disambiguationData":[OSD([subQ0]),TDD([makeQuery(id+"F6.imprint","IMPRINT",EDGE,{"disambiguationData":[TD([[makeQuery(id+"F6.imprint","INTERSECT",VERTEX,{"derivedFrom":[makeQuery(id+"F5.boolean.opBoolean","INTERSECT",EDGE,{"derivedFrom":[subQ5,makeQuery(id+"F5.opExtrude","SWEPT_FACE",FACE,{"disambiguationData":[OSD([sQuery(id+"F4.wireOp",EDGE,"E8.bottom")])]})]}),subQ0]}),-1.0],[makeQuery(id+"F6.imprint","INTERSECT",VERTEX,{"derivedFrom":[makeQuery(id+"F3.boolean.opBoolean","SPLIT",EDGE,{"disambiguationData":[TD([makeQuery(id+"F1.opExtrude","SWEPT_FACE",FACE,{"disambiguationData":[OSD([subQ1])]})])],"derivedFrom":makeQuery(id+"F1.opExtrude","CAP_EDGE",EDGE,{"disambiguationData":[OSD([subQ2])],"isStart":true})}),sQuery(id+"F6.wireOp",EDGE,"E12.top"),subQ0]}),1.0]])],"derivedFrom":subQ0})])],"isStart":true})]});}
            var Q17;
            {var subQ0=sQuery(id+"F0.wireOp",EDGE,"E0.left");var subQ1=sQuery(id+"F0.wireOp",EDGE,"E0.top");Q17=makeQuery(id+"F3.boolean.opBoolean","SPLIT",EDGE,{"disambiguationData":[TD([makeQuery(id+"F1.opExtrude","SWEPT_FACE",FACE,{"disambiguationData":[OSD([subQ0])]})])],"derivedFrom":makeQuery(id+"F1.opExtrude","CAP_EDGE",EDGE,{"disambiguationData":[OSD([subQ1])],"isStart":true})});}
            var Q18;
            {var subQ1=sQuery(id+"F0.wireOp",EDGE,"E0.left");var subQ2=sQuery(id+"F0.wireOp",EDGE,"E0.top");Q18=makeQuery(id+"F9.opChamfer","BLEND_EDGE",EDGE,{"blendedFrom":[makeQuery(id+"F1.opExtrude","SWEPT_EDGE",EDGE,{"disambiguationData":[OSD([subQ2,subQ1])]}),makeQuery(id+"F3.boolean.opBoolean","SPLIT",FACE,{"disambiguationData":[TD([makeQuery(id+"F1.opExtrude","SWEPT_FACE",FACE,{"disambiguationData":[OSD([subQ1])]})])],"derivedFrom":makeQuery(id+"F1.opExtrude","SWEPT_FACE",FACE,{"disambiguationData":[OSD([subQ2])]})})],"blendedInto":[makeQuery(id+"F3.boolean.opBoolean","SPLIT",FACE,{"disambiguationData":[TD([makeQuery(id+"F1.opExtrude","SWEPT_FACE",FACE,{"disambiguationData":[OSD([subQ1])]})])],"derivedFrom":makeQuery(id+"F1.opExtrude","SWEPT_FACE",FACE,{"disambiguationData":[OSD([subQ2])]})})]});}
            var Q19;
            {var subQ0=sQuery(id+"F0.wireOp",EDGE,"E0.bottom");Q19=makeQuery(id+"F9.opChamfer","BLEND_EDGE",EDGE,{"blendedFrom":[makeQuery(id+"F1.opExtrude","SWEPT_EDGE",EDGE,{"disambiguationData":[OSD([subQ0,sQuery(id+"F0.wireOp",EDGE,"E0.left")])]}),makeQuery(id+"F1.opExtrude","SWEPT_FACE",FACE,{"disambiguationData":[OSD([subQ0])]})],"blendedInto":[makeQuery(id+"F1.opExtrude","SWEPT_FACE",FACE,{"disambiguationData":[OSD([subQ0])]})]});}
            var Q20;
            {var subQ0=sQuery(id+"F0.wireOp",EDGE,"E0.bottom");Q20=makeQuery(id+"F9.opChamfer","BLEND_EDGE",EDGE,{"blendedFrom":[makeQuery(id+"F1.opExtrude","SWEPT_EDGE",EDGE,{"disambiguationData":[OSD([subQ0,sQuery(id+"F0.wireOp",EDGE,"E0.right")])]}),makeQuery(id+"F1.opExtrude","SWEPT_FACE",FACE,{"disambiguationData":[OSD([subQ0])]})],"blendedInto":[makeQuery(id+"F1.opExtrude","SWEPT_FACE",FACE,{"disambiguationData":[OSD([subQ0])]})]});}
            var Q21;
            {var subQ0=sQuery(id+"F0.wireOp",EDGE,"E0.right");var subQ2=sQuery(id+"F0.wireOp",EDGE,"E0.top");Q21=makeQuery(id+"F9.opChamfer","BLEND_EDGE",EDGE,{"blendedFrom":[makeQuery(id+"F1.opExtrude","SWEPT_EDGE",EDGE,{"disambiguationData":[OSD([subQ2,subQ0])]}),makeQuery(id+"F3.boolean.opBoolean","SPLIT",FACE,{"disambiguationData":[TD([makeQuery(id+"F1.opExtrude","SWEPT_FACE",FACE,{"disambiguationData":[OSD([subQ0])]})])],"derivedFrom":makeQuery(id+"F1.opExtrude","SWEPT_FACE",FACE,{"disambiguationData":[OSD([subQ2])]})})],"blendedInto":[makeQuery(id+"F3.boolean.opBoolean","SPLIT",FACE,{"disambiguationData":[TD([makeQuery(id+"F1.opExtrude","SWEPT_FACE",FACE,{"disambiguationData":[OSD([subQ0])]})])],"derivedFrom":makeQuery(id+"F1.opExtrude","SWEPT_FACE",FACE,{"disambiguationData":[OSD([subQ2])]})})]});}
            var Q22;
            Q22=makeQuery(id+"F1.opExtrude","CAP_EDGE",EDGE,{"disambiguationData":[OSD([sQuery(id+"F0.wireOp",EDGE,"E1.left")])],"isStart":false});
            var Q23;
            {var subQ0=sQuery(id+"F0.wireOp",EDGE,"E1.left");var subQ1=sQuery(id+"F0.wireOp",EDGE,"E1.top");Q23=makeQuery(id+"F10.opFillet","BLEND_EDGE",EDGE,{"blendedFrom":[makeQuery(id+"F1.opExtrude","SWEPT_EDGE",EDGE,{"disambiguationData":[OSD([subQ1,subQ0])]}),makeQuery(id+"F1.opExtrude","CAP_FACE",FACE,{"disambiguationData":[OSD([sQuery(id+"F0.wireOp",EDGE,"E0.bottom"),sQuery(id+"F0.wireOp",EDGE,"E0.top"),sQuery(id+"F0.wireOp",EDGE,"E0.left"),sQuery(id+"F0.wireOp",EDGE,"E0.right"),sQuery(id+"F0.wireOp",EDGE,"E1.bottom"),subQ1,subQ0,sQuery(id+"F0.wireOp",EDGE,"E1.right")])],"isStart":false})],"blendedInto":[makeQuery(id+"F1.opExtrude","CAP_FACE",FACE,{"disambiguationData":[OSD([sQuery(id+"F0.wireOp",EDGE,"E0.bottom"),sQuery(id+"F0.wireOp",EDGE,"E0.top"),sQuery(id+"F0.wireOp",EDGE,"E0.left"),sQuery(id+"F0.wireOp",EDGE,"E0.right"),sQuery(id+"F0.wireOp",EDGE,"E1.bottom"),subQ1,subQ0,sQuery(id+"F0.wireOp",EDGE,"E1.right")])],"isStart":false})]});}
            var Q24;
            Q24=makeQuery(id+"F1.opExtrude","CAP_EDGE",EDGE,{"disambiguationData":[OSD([sQuery(id+"F0.wireOp",EDGE,"E1.bottom")])],"isStart":true});
            chamfer(context, id + "F11", {"entities" : qUnion([Q0, Q1, Q2, Q3, Q4, Q5, Q6, Q7, Q8, Q9, Q10, Q11, Q12, Q13, Q14, Q15, Q16, Q17, Q18, Q19, Q20, Q21, Q22, Q23, Q24]), "width" : 1 * mm, "tangentPropagation" : true});
        }
        {
            var Q0;
            Q0=makeQuery(id+"F1.opExtrude","CAP_FACE",FACE,{"disambiguationData":[OSD([sQuery(id+"F0.wireOp",EDGE,"E0.bottom"),sQuery(id+"F0.wireOp",EDGE,"E0.top"),sQuery(id+"F0.wireOp",EDGE,"E0.left"),sQuery(id+"F0.wireOp",EDGE,"E0.right")])],"isStart":false});
            var sketch = newSketch(context, id + "F12", { "sketchPlane" : qUnion([Q0])});
            skCircle(sketch, "E14", {"center": v(47.37, 84) * mm, "radius": 3 * mm});
            skCircle(sketch, "E15.0.1.0", {"center": v(47.37, 119) * mm, "radius": 3 * mm});
            skCircle(sketch, "E15.1.0.0", {"center": v(87.37, 84) * mm, "radius": 3 * mm});
            skCircle(sketch, "E15.1.1.0", {"center": v(87.37, 119) * mm, "radius": 3 * mm});
            skLineSegment(sketch, "E15.direction1", {"start": v(47.37, 84) * mm, "end": v(87.37, 84) * mm, "construction": true});
            skLineSegment(sketch, "E15.direction2", {"start": v(47.37, 84) * mm, "end": v(47.37, 119) * mm, "construction": true});
            skCircle(sketch, "E16", {"center": v(47.37, 84) * mm, "radius": 1 * mm});
            skCircle(sketch, "E17.0.1.0", {"center": v(47.37, 119) * mm, "radius": 1 * mm});
            skCircle(sketch, "E17.1.0.0", {"center": v(87.37, 84) * mm, "radius": 1 * mm});
            skCircle(sketch, "E17.1.1.0", {"center": v(87.37, 119) * mm, "radius": 1 * mm});
            skLineSegment(sketch, "E18.bottom", {"start": v(44.37, 119) * mm, "end": v(50.37, 119) * mm});
            skLineSegment(sketch, "E18.top", {"start": v(44.37, 84) * mm, "end": v(50.37, 84) * mm});
            skLineSegment(sketch, "E18.left", {"start": v(44.37, 119) * mm, "end": v(44.37, 84) * mm});
            skLineSegment(sketch, "E18.right", {"start": v(50.37, 119) * mm, "end": v(50.37, 84) * mm});
            skLineSegment(sketch, "E19.bottom", {"start": v(84.37, 119) * mm, "end": v(90.37, 119) * mm});
            skLineSegment(sketch, "E19.top", {"start": v(84.37, 84) * mm, "end": v(90.37, 84) * mm});
            skLineSegment(sketch, "E19.left", {"start": v(84.37, 119) * mm, "end": v(84.37, 84) * mm});
            skLineSegment(sketch, "E19.right", {"start": v(90.37, 119) * mm, "end": v(90.37, 84) * mm});
            skSolve(sketch);
        }
        {
            var Q0;
            Q0=makeQuery(id+"F12.imprint","IMPRINT",FACE,{"disambiguationData":[TD([[makeQuery(id+"F12.imprint","IMPRINT",EDGE,{"derivedFrom":sQuery(id+"F12.wireOp",EDGE,"E15.0.1.0")}),1.0]])]});
            var Q1;
            Q1=makeQuery(id+"F12.imprint","IMPRINT",FACE,{"disambiguationData":[TD([[makeQuery(id+"F12.imprint","IMPRINT",EDGE,{"derivedFrom":sQuery(id+"F12.wireOp",EDGE,"E14")}),1.0]])]});
            var Q2;
            Q2=makeQuery(id+"F12.imprint","IMPRINT",FACE,{"disambiguationData":[TD([[makeQuery(id+"F12.imprint","IMPRINT",EDGE,{"derivedFrom":sQuery(id+"F12.wireOp",EDGE,"E15.1.0.0")}),1.0]])]});
            var Q3;
            Q3=makeQuery(id+"F12.imprint","IMPRINT",FACE,{"disambiguationData":[TD([[makeQuery(id+"F12.imprint","IMPRINT",EDGE,{"derivedFrom":sQuery(id+"F12.wireOp",EDGE,"E15.1.1.0")}),1.0]])]});
            var Q4;
            Q4=makeQuery(id+"F12.imprint","IMPRINT",FACE,{"disambiguationData":[TD([[makeQuery(id+"F12.imprint","IMPRINT",EDGE,{"derivedFrom":sQuery(id+"F12.wireOp",EDGE,"E17.0.1.0")}),1.0]])]});
            var Q5;
            Q5=makeQuery(id+"F12.imprint","IMPRINT",FACE,{"disambiguationData":[TD([[makeQuery(id+"F12.imprint","IMPRINT",EDGE,{"derivedFrom":sQuery(id+"F12.wireOp",EDGE,"E16")}),1.0]])]});
            var Q6;
            Q6=makeQuery(id+"F12.imprint","IMPRINT",FACE,{"disambiguationData":[TD([[makeQuery(id+"F12.imprint","IMPRINT",EDGE,{"derivedFrom":sQuery(id+"F12.wireOp",EDGE,"E17.1.1.0")}),1.0]])]});
            var Q7;
            Q7=makeQuery(id+"F12.imprint","IMPRINT",FACE,{"disambiguationData":[TD([[makeQuery(id+"F12.imprint","IMPRINT",EDGE,{"derivedFrom":sQuery(id+"F12.wireOp",EDGE,"E17.1.0.0")}),1.0]])]});
            var Q8;
            {var subQ0=sQuery(id+"F12.wireOp",EDGE,"E18.left");Q8=makeQuery(id+"F12.imprint","IMPRINT",FACE,{"disambiguationData":[TD([[makeQuery(id+"F12.imprint","IMPRINT",EDGE,{"derivedFrom":subQ0}),1.0]])]});}
            var Q9;
            {var subQ0=sQuery(id+"F12.wireOp",EDGE,"E19.left");Q9=makeQuery(id+"F12.imprint","IMPRINT",FACE,{"disambiguationData":[TD([[makeQuery(id+"F12.imprint","IMPRINT",EDGE,{"derivedFrom":subQ0}),1.0]])]});}
            var Q10;
            Q10=sQuery(id+"F12.wireOp",EDGE,"E17.0.1.0");
            var Q11;
            Q11=sQuery(id+"F12.wireOp",EDGE,"E15.0.1.0");
            extrude(context, id + "F13", {"entities" : qUnion([Q0, Q1, Q2, Q3, Q4, Q5, Q6, Q7, Q8, Q9]), "operationType" : NewBodyOperationType.REMOVE, "surfaceOperationType" : NewSurfaceOperationType.ADD, "surfaceEntities" : qUnion([Q10, Q11]), "oppositeDirection" : true, "depth" : 18 * mm, "offsetDistance" : 25 * mm});
        }
    });
